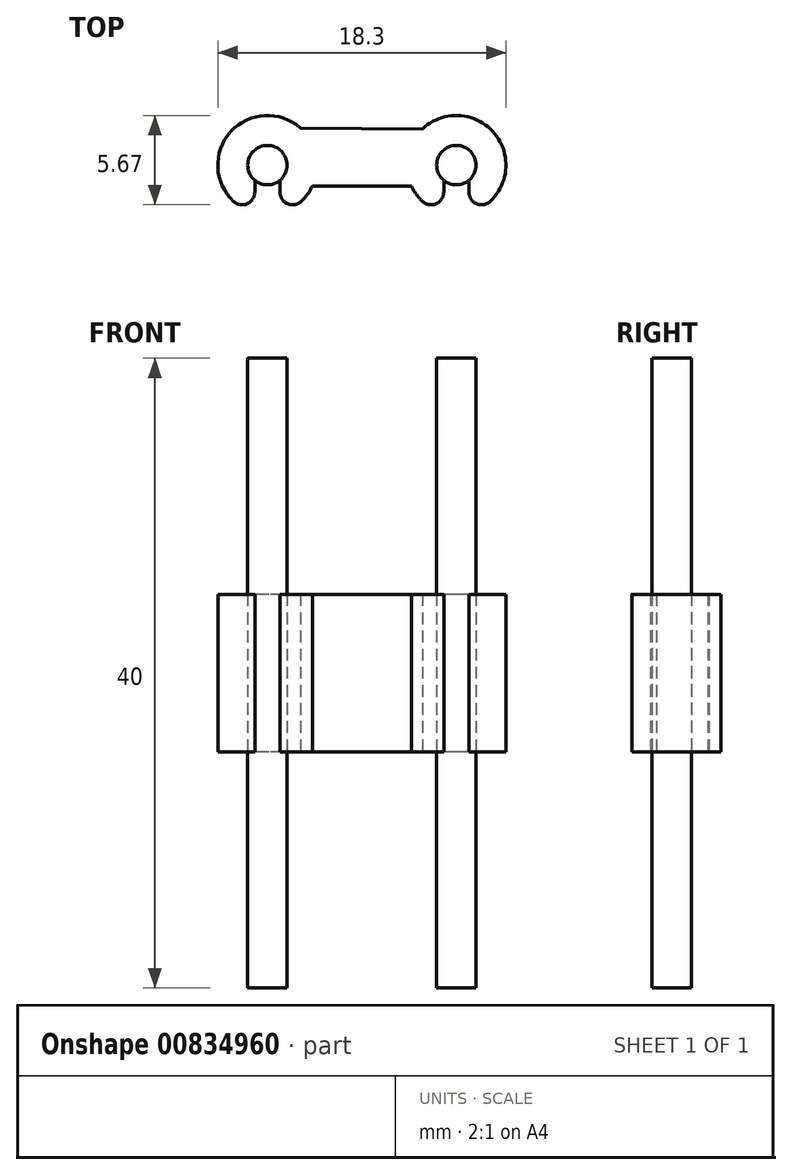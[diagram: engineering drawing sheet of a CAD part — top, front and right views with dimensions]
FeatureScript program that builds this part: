
annotation { "Feature Type Name" : "Feature", "Feature Type Description" : "" }
export const myFeature = defineFeature(function(context is Context, id is Id, definition is map)
    precondition{}
    {
        {
            var Q0;
            Q0=qCreatedBy(makeId("Top.planeOp"),FACE);
            var sketch = newSketch(context, id + "F0", { "sketchPlane" : qUnion([Q0])});
            skCircle(sketch, "E0", {"center": v(0, 0) * mm, "radius": 1.25 * mm});
            skPoint(sketch, "E1", {"position": v(12, 0) * mm});
            skCircle(sketch, "E2", {"center": v(12, 0) * mm, "radius": 1.25 * mm});
            skSolve(sketch);
        }
        {
            var Q0;
            Q0=makeQuery(id+"F0.imprint","IMPRINT",FACE,{"disambiguationData":[TD([[makeQuery(id+"F0.imprint","IMPRINT",EDGE,{"derivedFrom":sQuery(id+"F0.wireOp",EDGE,"E0")}),1.0]])]});
            var Q1;
            Q1=makeQuery(id+"F0.imprint","IMPRINT",FACE,{"disambiguationData":[TD([[makeQuery(id+"F0.imprint","IMPRINT",EDGE,{"derivedFrom":sQuery(id+"F0.wireOp",EDGE,"E2")}),1.0]])]});
            extrude(context, id + "F1", {"entities" : qUnion([Q0, Q1]), "endBound" : BoundingType.SYMMETRIC, "depth" : 40 * mm, "offsetDistance" : 25 * mm});
        }
        {
            var Q0;
            Q0=qCreatedBy(makeId("Top.planeOp"),FACE);
            var sketch = newSketch(context, id + "F2", { "sketchPlane" : qUnion([Q0])});
            skCircle(sketch, "E3.0", {"center": v(0, 0) * mm, "radius": 1.25 * mm});
            skCircle(sketch, "E4.0", {"center": v(12, 0) * mm, "radius": 1.25 * mm});
            skArc(sketch, "E5.0", {"start": v(2.09, 2.36) * mm, "mid": v(-3.09, -0.64) * mm, "end": v(2.85, -1.34) * mm});
            skArc(sketch, "E6.0", {"start": v(9.15, -1.34) * mm, "mid": v(15.1, -0.6) * mm, "end": v(9.84, 2.3) * mm});
            skLineSegment(sketch, "E7", {"start": v(0, 7.62) * mm, "end": v(0, -7.13) * mm, "construction": true});
            skLineSegment(sketch, "E8", {"start": v(12, 0) * mm, "end": v(12, -9.16) * mm, "construction": true});
            skPoint(sketch, "E9", {"position": v(12.8, -0.96) * mm});
            skLineSegment(sketch, "E10", {"start": v(12.8, -0.96) * mm, "end": v(12.8, -3.05) * mm});
            skLineSegment(sketch, "E11.MirrorCS", {"start": v(11.2, -0.96) * mm, "end": v(11.2, -3.05) * mm});
            skLineSegment(sketch, "E12", {"start": v(12.8, -0.96) * mm, "end": v(0, -0.96) * mm, "construction": true});
            skPoint(sketch, "E13", {"position": v(0.8, -0.96) * mm});
            skLineSegment(sketch, "E14", {"start": v(0.8, -0.96) * mm, "end": v(0.8, -3.05) * mm});
            skLineSegment(sketch, "E15.MirrorCS", {"start": v(-0.8, -0.96) * mm, "end": v(-0.8, -3.05) * mm});
            skLineSegment(sketch, "E16", {"start": v(3, -0.96) * mm, "end": v(3, -0.96) * mm});
            skLineSegment(sketch, "E17", {"start": v(2.09, 2.36) * mm, "end": v(9.84, 2.3) * mm});
            skLineSegment(sketch, "E18", {"start": v(9.15, -1.34) * mm, "end": v(2.85, -1.34) * mm});
            skSolve(sketch);
        }
        {
            var Q0;
            {var subQ4=sQuery(id+"F2.wireOp",EDGE,"E10");Q0=makeQuery(id+"F2.imprint","IMPRINT",FACE,{"disambiguationData":[TD([[makeQuery(id+"F2.imprint","IMPRINT",EDGE,{"derivedFrom":subQ4}),1.0]])]});}
            extrude(context, id + "F3", {"entities" : qUnion([Q0]), "endBound" : BoundingType.SYMMETRIC, "depth" : 10 * mm, "offsetDistance" : 25 * mm});
        }
        {
            var Q0;
            Q0=makeQuery(id+"F3.opExtrude","SWEPT_EDGE",EDGE,{"disambiguationData":[OSD([sQuery(id+"F2.wireOp",EDGE,"E5.0"),sQuery(id+"F2.wireOp",EDGE,"E15.MirrorCS")])]});
            var Q1;
            Q1=makeQuery(id+"F3.opExtrude","SWEPT_EDGE",EDGE,{"disambiguationData":[OSD([sQuery(id+"F2.wireOp",EDGE,"E5.0"),sQuery(id+"F2.wireOp",EDGE,"E14")])]});
            var Q2;
            Q2=makeQuery(id+"F3.opExtrude","SWEPT_EDGE",EDGE,{"disambiguationData":[OSD([sQuery(id+"F2.wireOp",EDGE,"E6.0"),sQuery(id+"F2.wireOp",EDGE,"E11.MirrorCS")])]});
            var Q3;
            Q3=makeQuery(id+"F3.opExtrude","SWEPT_EDGE",EDGE,{"disambiguationData":[OSD([sQuery(id+"F2.wireOp",EDGE,"E6.0"),sQuery(id+"F2.wireOp",EDGE,"E10")])]});
            fillet(context, id + "F4", {"entities" : qUnion([Q0, Q1, Q2, Q3]), "radius" : .8 * mm, "tangentPropagation" : true, "allowEdgeOverflow" : false});
        }
    });
